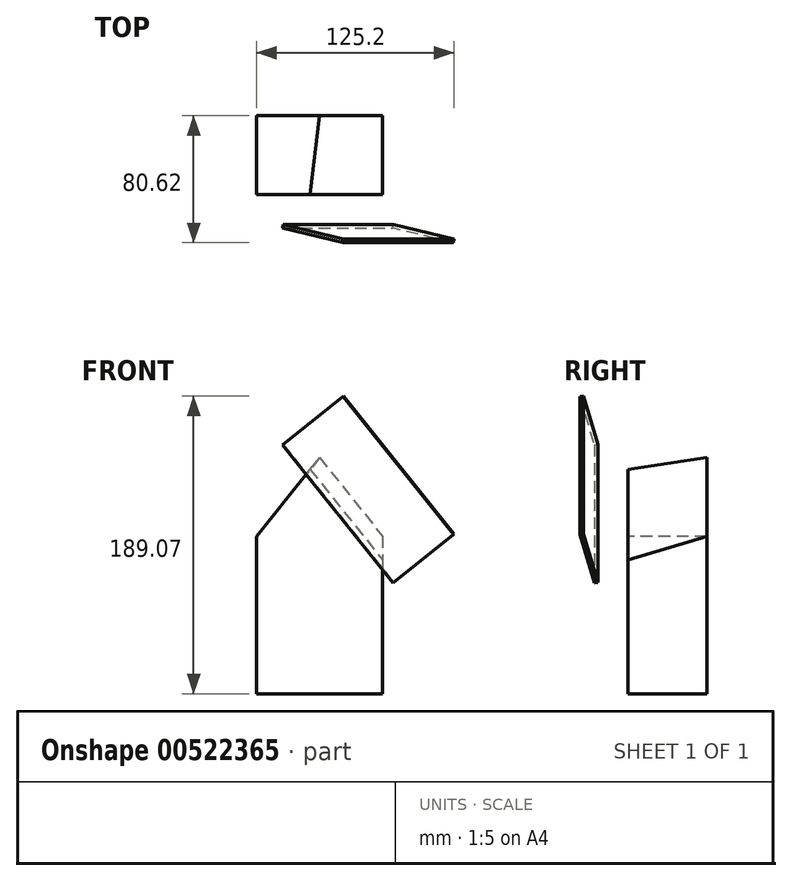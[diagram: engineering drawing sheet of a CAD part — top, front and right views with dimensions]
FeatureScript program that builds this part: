
annotation { "Feature Type Name" : "Feature", "Feature Type Description" : "" }
export const myFeature = defineFeature(function(context is Context, id is Id, definition is map)
    precondition{}
    {
        {
            var Q0;
            Q0=qCreatedBy(makeId("Top.planeOp"),FACE);
            var sketch = newSketch(context, id + "F0", { "sketchPlane" : qUnion([Q0])});
            skLineSegment(sketch, "E0.bottom", {"start": v(40, -25) * mm, "end": v(-40, -25) * mm});
            skLineSegment(sketch, "E0.top", {"start": v(40, 25) * mm, "end": v(-40, 25) * mm});
            skLineSegment(sketch, "E0.left", {"start": v(40, -25) * mm, "end": v(40, 25) * mm});
            skLineSegment(sketch, "E0.right", {"start": v(-40, -25) * mm, "end": v(-40, 25) * mm});
            skPoint(sketch, "E0.middle", {"position": v(0, 0) * mm});
            skSolve(sketch);
        }
        {
            var Q0;
            Q0=makeQuery(id+"F0.imprint","IMPRINT",FACE,{"disambiguationData":[TD([[makeQuery(id+"F0.imprint","IMPRINT",EDGE,{"derivedFrom":sQuery(id+"F0.wireOp",EDGE,"E0.bottom")}),-1.0]])]});
            extrude(context, id + "F1", {"entities" : qUnion([Q0]), "depth" : 150 * mm, "offsetDistance" : 25 * mm});
        }
        {
            var Q0;
            Q0=makeQuery(id+"F1.opExtrude","SWEPT_FACE",FACE,{"disambiguationData":[OSD([sQuery(id+"F0.wireOp",EDGE,"E0.bottom")])]});
            var sketch = newSketch(context, id + "F2", { "sketchPlane" : qUnion([Q0])});
            skPoint(sketch, "E1", {"position": v(-40, 100) * mm});
            skPoint(sketch, "E2", {"position": v(0, 150) * mm});
            skLineSegment(sketch, "E3", {"start": v(-40, 100) * mm, "end": v(0, 150) * mm});
            skLineSegment(sketch, "E4", {"start": v(-40, 150) * mm, "end": v(-40, 100) * mm});
            skSolve(sketch);
        }
        {
            var Q0;
            {var subQ0=sQuery(id+"F2.wireOp",EDGE,"E3");Q0=makeQuery(id+"F2.imprint","IMPRINT",FACE,{"disambiguationData":[TD([[makeQuery(id+"F2.imprint","IMPRINT",EDGE,{"derivedFrom":subQ0}),1.0]])]});}
            extrude(context, id + "F3", {"entities" : qUnion([Q0]), "operationType" : NewBodyOperationType.REMOVE, "endBound" : BoundingType.UP_TO_NEXT, "oppositeDirection" : true, "depth" : 25 * mm, "offsetDistance" : 25 * mm});
        }
        {
            var Q0;
            Q0=makeQuery(id+"F1.opExtrude","SWEPT_FACE",FACE,{"disambiguationData":[OSD([sQuery(id+"F0.wireOp",EDGE,"E0.left")])]});
            var sketch = newSketch(context, id + "F4", { "sketchPlane" : qUnion([Q0])});
            skPoint(sketch, "E5", {"position": v(-25, 85) * mm});
            skPoint(sketch, "E6", {"position": v(25, 100) * mm});
            skSolve(sketch);
        }
        {
            var Q0;
            Q0 = qBodyType(qCreatedBy(id + "F4" ,EDGE), BodyType.WIRE);
            var Q1;
            Q1=sQuery(id+"F4.wireOp",VERTEX,"E5");
            var Q2;
            Q2=sQuery(id+"F4.wireOp",VERTEX,"E6");
            var Q3;
            Q3=makeQuery(id+"F3.boolean.opBoolean","COPY",VERTEX,{"derivedFrom":makeQuery(id+"F3.opExtrude","CAP_VERTEX",VERTEX,{"disambiguationData":[OSD([sQuery(id+"F0.wireOp",EDGE,"E0.bottom"),sQuery(id+"F0.wireOp",EDGE,"E0.top"),sQuery(id+"F2.wireOp",EDGE,"E3")])],"isStart":false})});
            cPlane(context, id + "F5", {"entities" : qUnion([Q0, Q1, Q2, Q3]), "cplaneType" : CPlaneType.THREE_POINT, "offset" : 25 * mm, "width" : 150 * mm, "height" : 150 * mm});
        }
        {
            var Q0;
            Q0=qCreatedBy(id+"F5.planeOp",FACE);
            var sketch = newSketch(context, id + "F6", { "sketchPlane" : qUnion([Q0])});
            skLineSegment(sketch, "E7.bottom", {"start": v(30.82, 138.2) * mm, "end": v(28.35, 138.2) * mm});
            skLineSegment(sketch, "E7.top", {"start": v(30.82, 26.01) * mm, "end": v(28.35, 26.01) * mm});
            skLineSegment(sketch, "E7.left", {"start": v(30.82, 138.2) * mm, "end": v(30.82, 26.01) * mm});
            skLineSegment(sketch, "E7.right", {"start": v(28.35, 138.2) * mm, "end": v(28.35, 26.01) * mm});
            skSolve(sketch);
        }
        {
            var Q0;
            Q0=makeQuery(id+"F6.imprint","IMPRINT",FACE,{"disambiguationData":[TD([[makeQuery(id+"F6.imprint","IMPRINT",EDGE,{"derivedFrom":sQuery(id+"F6.wireOp",EDGE,"E7.bottom")}),1.0]])]});
            extrude(context, id + "F7", {"entities" : qUnion([Q0]), "oppositeDirection" : true, "depth" : 50 * mm, "offsetDistance" : 25 * mm});
        }
        {
            var Q0;
            Q0=makeQuery(id+"F7.opExtrude","SWEPT_FACE",FACE,{"disambiguationData":[OSD([sQuery(id+"F6.wireOp",EDGE,"E7.right")])]});
            extrude(context, id + "F8", {"entities" : qUnion([Q0]), "operationType" : NewBodyOperationType.REMOVE, "depth" : 100 * mm, "offsetDistance" : 25 * mm});
        }
    });
